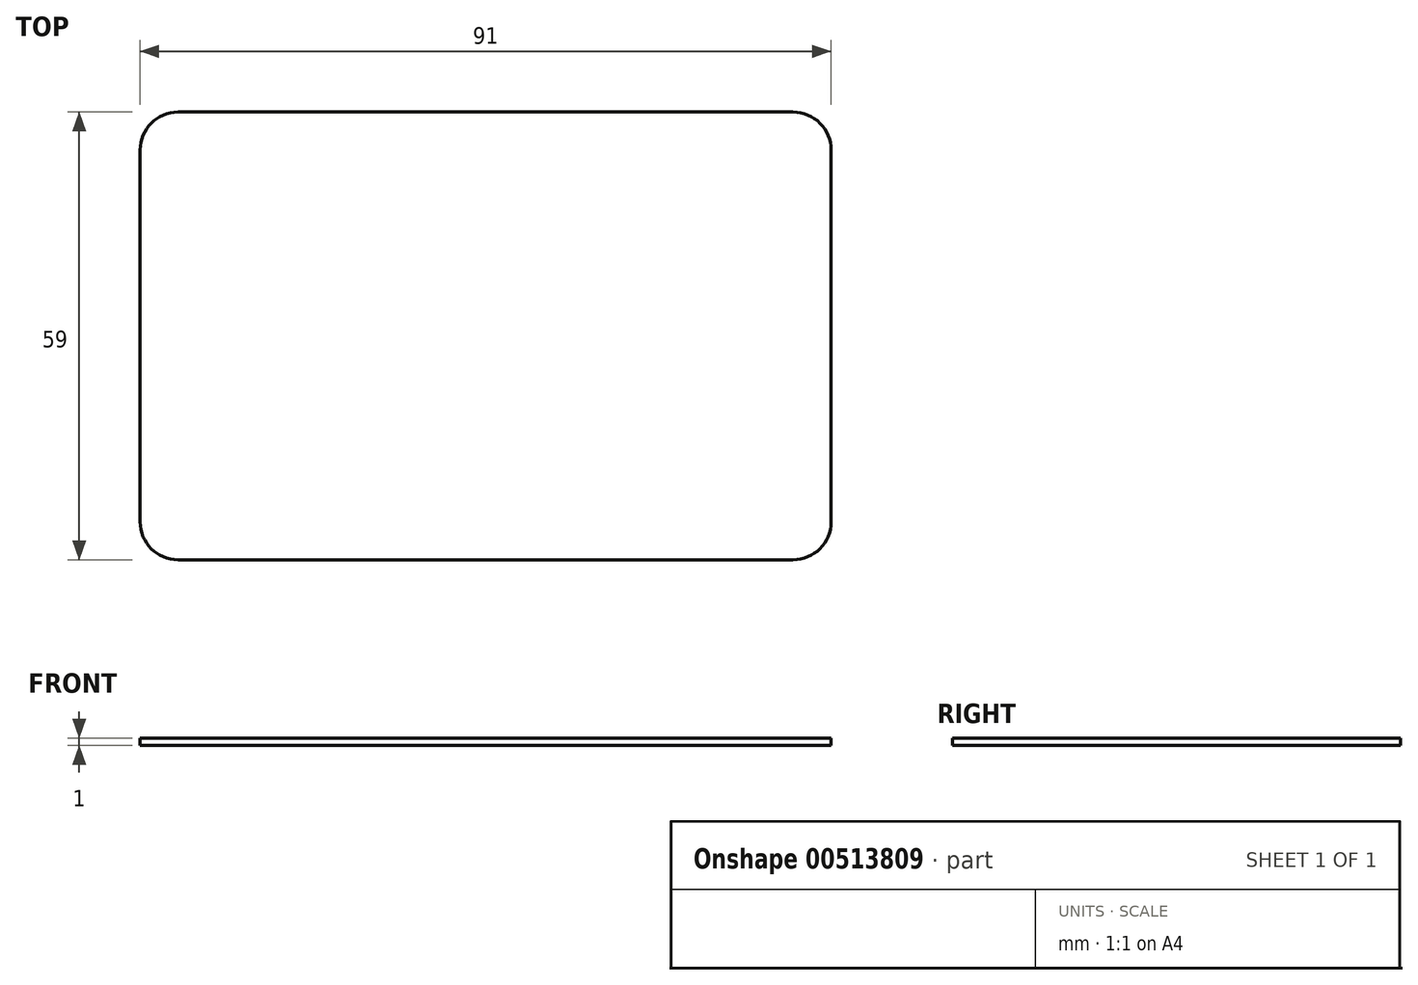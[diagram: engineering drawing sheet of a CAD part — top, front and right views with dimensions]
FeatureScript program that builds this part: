
annotation { "Feature Type Name" : "Feature", "Feature Type Description" : "" }
export const myFeature = defineFeature(function(context is Context, id is Id, definition is map)
    precondition{}
    {
        {
            var Q0;
            Q0=qCreatedBy(makeId("Top.planeOp"),FACE);
            var sketch = newSketch(context, id + "F0", { "sketchPlane" : qUnion([Q0])});
            skLineSegment(sketch, "E0.bottom", {"start": v(-19.09, 37.27) * mm, "end": v(61.91, 37.27) * mm});
            skLineSegment(sketch, "E0.top", {"start": v(-19.09, -21.73) * mm, "end": v(61.91, -21.73) * mm});
            skLineSegment(sketch, "E0.left", {"start": v(-24.09, 32.27) * mm, "end": v(-24.09, -16.73) * mm});
            skLineSegment(sketch, "E0.right", {"start": v(66.91, 32.27) * mm, "end": v(66.91, -16.73) * mm});
            skPoint(sketch, "E1.visualSharp", {"position": v(66.91, 37.27) * mm});
            skArc(sketch, "E1.filletArc", {"start": v(66.91, 32.27) * mm, "mid": v(65.45, 35.8) * mm, "end": v(61.91, 37.27) * mm});
            skPoint(sketch, "E2.visualSharp", {"position": v(66.91, -21.73) * mm});
            skArc(sketch, "E2.filletArc", {"start": v(61.91, -21.73) * mm, "mid": v(65.45, -20.27) * mm, "end": v(66.91, -16.73) * mm});
            skPoint(sketch, "E3.visualSharp", {"position": v(-24.09, -21.73) * mm});
            skArc(sketch, "E3.filletArc", {"start": v(-24.09, -16.73) * mm, "mid": v(-22.62, -20.27) * mm, "end": v(-19.09, -21.73) * mm});
            skPoint(sketch, "E4.visualSharp", {"position": v(-24.09, 37.27) * mm});
            skArc(sketch, "E4.filletArc", {"start": v(-19.09, 37.27) * mm, "mid": v(-22.62, 35.8) * mm, "end": v(-24.09, 32.27) * mm});
            skSolve(sketch);
        }
        {
            var Q0;
            Q0 = qSketchRegion(id + "F0", true);
            extrude(context, id + "F1", {"entities" : qUnion([Q0]), "depth" : 1 * mm});
        }
    });
